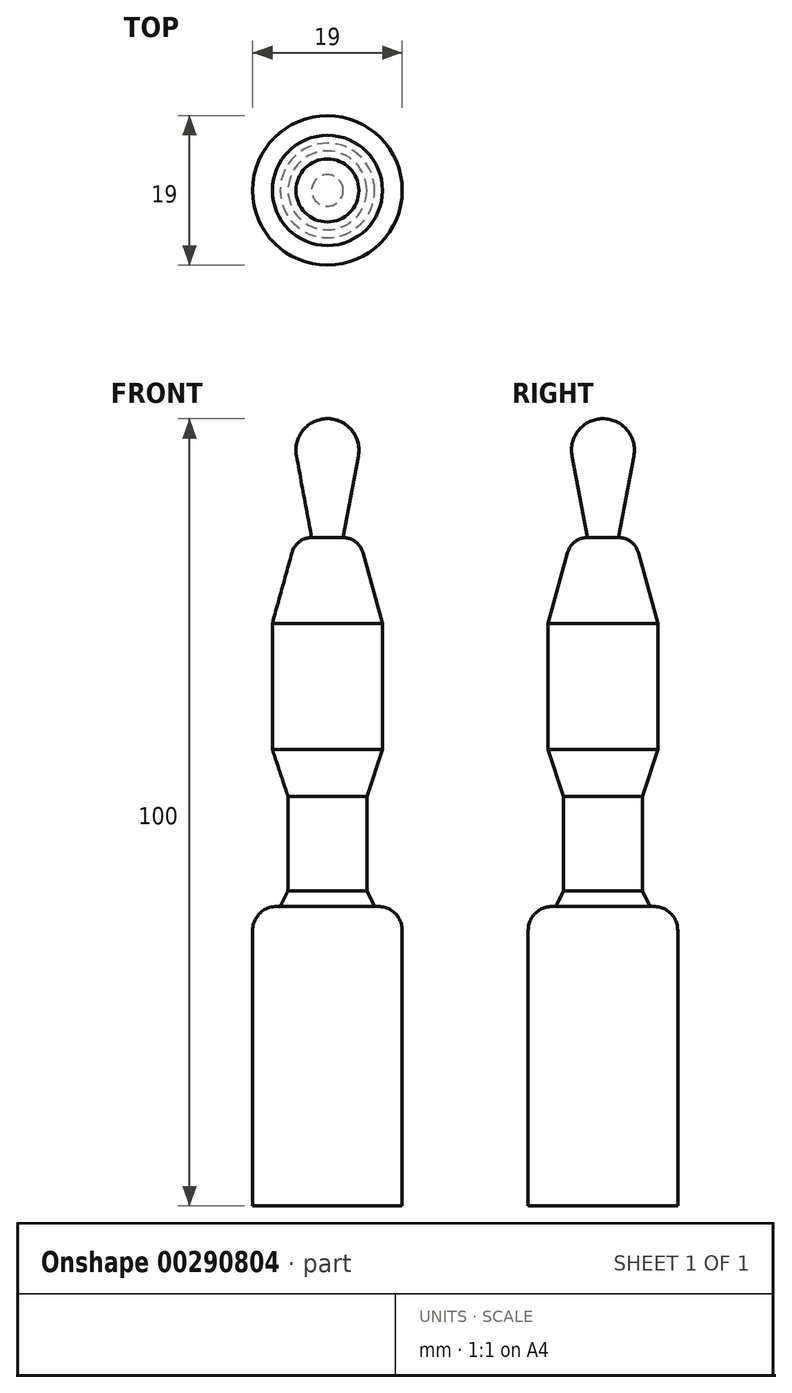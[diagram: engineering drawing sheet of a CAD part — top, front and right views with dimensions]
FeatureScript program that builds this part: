
annotation { "Feature Type Name" : "Feature", "Feature Type Description" : "" }
export const myFeature = defineFeature(function(context is Context, id is Id, definition is map)
    precondition{}
    {
        {
            var Q0;
            Q0=qCreatedBy(makeId("Front.planeOp"),FACE);
            var sketch = newSketch(context, id + "F0", { "sketchPlane" : qUnion([Q0])});
            skLineSegment(sketch, "E0", {"start": v(9.5, 0) * mm, "end": v(9.5, 35) * mm});
            skLineSegment(sketch, "E1", {"start": v(5, 40) * mm, "end": v(5, 52) * mm});
            skLineSegment(sketch, "E2", {"start": v(5, 52) * mm, "end": v(7, 58) * mm});
            skLineSegment(sketch, "E3", {"start": v(7, 58) * mm, "end": v(7, 74) * mm});
            skLineSegment(sketch, "E4", {"start": v(7, 74) * mm, "end": v(4.5, 83) * mm});
            skLineSegment(sketch, "E5", {"start": v(9.5, 0) * mm, "end": v(0, 0) * mm});
            skLineSegment(sketch, "E6", {"start": v(0, 0) * mm, "end": v(0, 100) * mm});
            skArc(sketch, "E7", {"start": v(9.5, 35) * mm, "mid": v(8.44, 37.3) * mm, "end": v(6, 38) * mm});
            skLineSegment(sketch, "E8", {"start": v(6, 38) * mm, "end": v(5, 40) * mm});
            skArc(sketch, "E9", {"start": v(3.93, 95.27) * mm, "mid": v(3.08, 98.56) * mm, "end": v(0, 100) * mm});
            skLineSegment(sketch, "E10", {"start": v(3.93, 95.27) * mm, "end": v(2, 84.9) * mm});
            skArc(sketch, "E11", {"start": v(4.5, 83) * mm, "mid": v(3.57, 84.37) * mm, "end": v(2, 84.9) * mm});
            skSolve(sketch);
        }
        {
            var Q0;
            Q0=makeQuery(id+"F0.imprint","IMPRINT",FACE,{"disambiguationData":[TD([[makeQuery(id+"F0.imprint","IMPRINT",EDGE,{"derivedFrom":sQuery(id+"F0.wireOp",EDGE,"E0")}),1.0]])]});
            var Q1;
            Q1=sQuery(id+"F0.wireOp",EDGE,"E6");
            revolve(context, id + "F1", {"entities" : qUnion([Q0]), "axis" : qUnion([Q1]), "revolveType" : RevolveType.FULL});
        }
    });
